# Revit family: IS_TonicII_R4308_BIM_DE
name_source: partatom
category: Plumbing Fixtures
revit_build: Autodesk Revit MEP 2016 (Build: 20161004_0715(x64)
units: mm (PartAtom-declared; Revit-internal decimal feet)

## family parameters
Always vertical = No
Cut with Voids When Loaded = No
OmniClass Number = 23.45.05.14.17.11
OmniClass Title = Shower Compartments
Part Type = Normal
Room Calculation Point = No
Round Connector Dimension = Use Diameter
Shared = No
Work Plane-Based = No

## types (5) — shared parameters
Accessories = www.idealstandard.de\ersatzteile
Assembly Code = C1030200
AssetType = Fest
BIMobject category = Storage
BOSUseNativeGeometries = 1
Brand = Ideal Standard
Brand url = http://www.idealstandard.de
CurrencyUnit = €
CurrentRevision = 1
Date of publishing = 15/09/2017
DurationUnit = Jahr
EAN code = https://3391500571808
Edition number = 1
ExpectedLife = 25
Features = TONIC II side unit 350x440mm, 1 door
IFC Classification = Sanitary Terminal
Installation instructions = http://www.idealstandard.de
InstallationInstructions = www.idealstandard.de\produkte
Manufacturer = www.idealstandard.de\produkte
Manufacturer name = Ideal Standard
ManufacturerURL = http://www.idealstandard.de
NettWeight = 14 kg
Nominal height = 600
Nominal width = 350
NominalHeight = 600 mm
NominalLength = 445 mm
NominalWidth = 353 mm
Product Guid = 19a285cb-1c8e-4356-9fa2-963cc1d2f6f5
Product SKU = R4308
Product data url = https://bimobject.com
Product family = TONIC II
Product group = Furniture
Product name = TONIC II side unit 350x440mm, 1 door
Product url = http://www.idealstandard.de
ProductInformation = www.idealstandard.de\produkte
QR code = http://bimobject.com
Shape = Rectangular
Size = 600 x 445 x 353mm
Space = Intern
SpareParts = www.idealstandard.de/ersatzteile
Technical description = http://www.idealstandard.de
URL = http://www.idealstandard.de
Uniclass2015Code = Pr_40_30_78_03
Uniclass2015Title = Bathroom cabinets
Uniclass2015Version = Products v1.1
Version = 1
VolumeUnits = Litres
Weight Net (Kg) = 14
zero-valued in all types: Cost

## per-type parameters (varying)
| type | BarCode | Color | Description | Finish | MainColor | Model | ModelNumber | ModelReference |
| R4308FE - IS Seitenschrank TONIC II,A/re.o.li.,1T. ,350x440x600mm, Eiche grau Dekor | 3391500571846 | Wood Light Grey | R4308FE TONIC II side unit 350x440mm, 1 door | Wood Light Grey | Wood Light Grey | R4308FE | R4308FE | R4308FE TONIC II side unit 350x440mm, 1 door |
| R4308FC - IS Seitenschrank TONIC II,A/re.o.li.,1T. ,350x440x600mm, Hgl.hellbraun lackiert | 3391500571822 | Glossy Light Brown | R4308FC TONIC II side unit 350x440mm, 1 door | Glossy Light Brown | Glossy Light Brown | R4308FC | R4308FC | R4308FC TONIC II side unit 350x440mm, 1 door |
| R4308FA - IS Seitenschrank TONIC II,A/re.o.li.,1T. ,350x440x600mm, Hgl.hellgrau lackiert | 3391500571815 | Glossy Light Grey | R4308FA TONIC II side unit 350x440mm, 1 door | Glossy Light Grey | Glossy Light Grey | R4308FA | R4308FA | R4308FA TONIC II side unit 350x440mm, 1 door |
| R4308WG - IS Seitenschrank TONIC II,A/re.o.li.,1T. ,350x440x600mm, Hgl.weiß lackiert | 3391500571808 | Glossy White | R4308WG TONIC II side unit 350x440mm, 1 door | Glossy White | Glossy White | R4308WG | R4308WG | R4308WG TONIC II side unit 350x440mm, 1 door |
| R4308FF - IS Seitenschrank TONIC II,A/re.o.li.,1T. ,350x440x600mm, Pinie hell Dekor | 3391500571839 | Wood Light Brown | R4308FF TONIC II side unit 350x440mm, 1 door | Wood Light Brown | Wood Light Brown | R4308FF | R4308FF | R4308FF TONIC II side unit 350x440mm, 1 door |

## geometry (parser evidence)
native form markers: Blend x4, Sweep x2
no freeform markers — native parametric forms only
